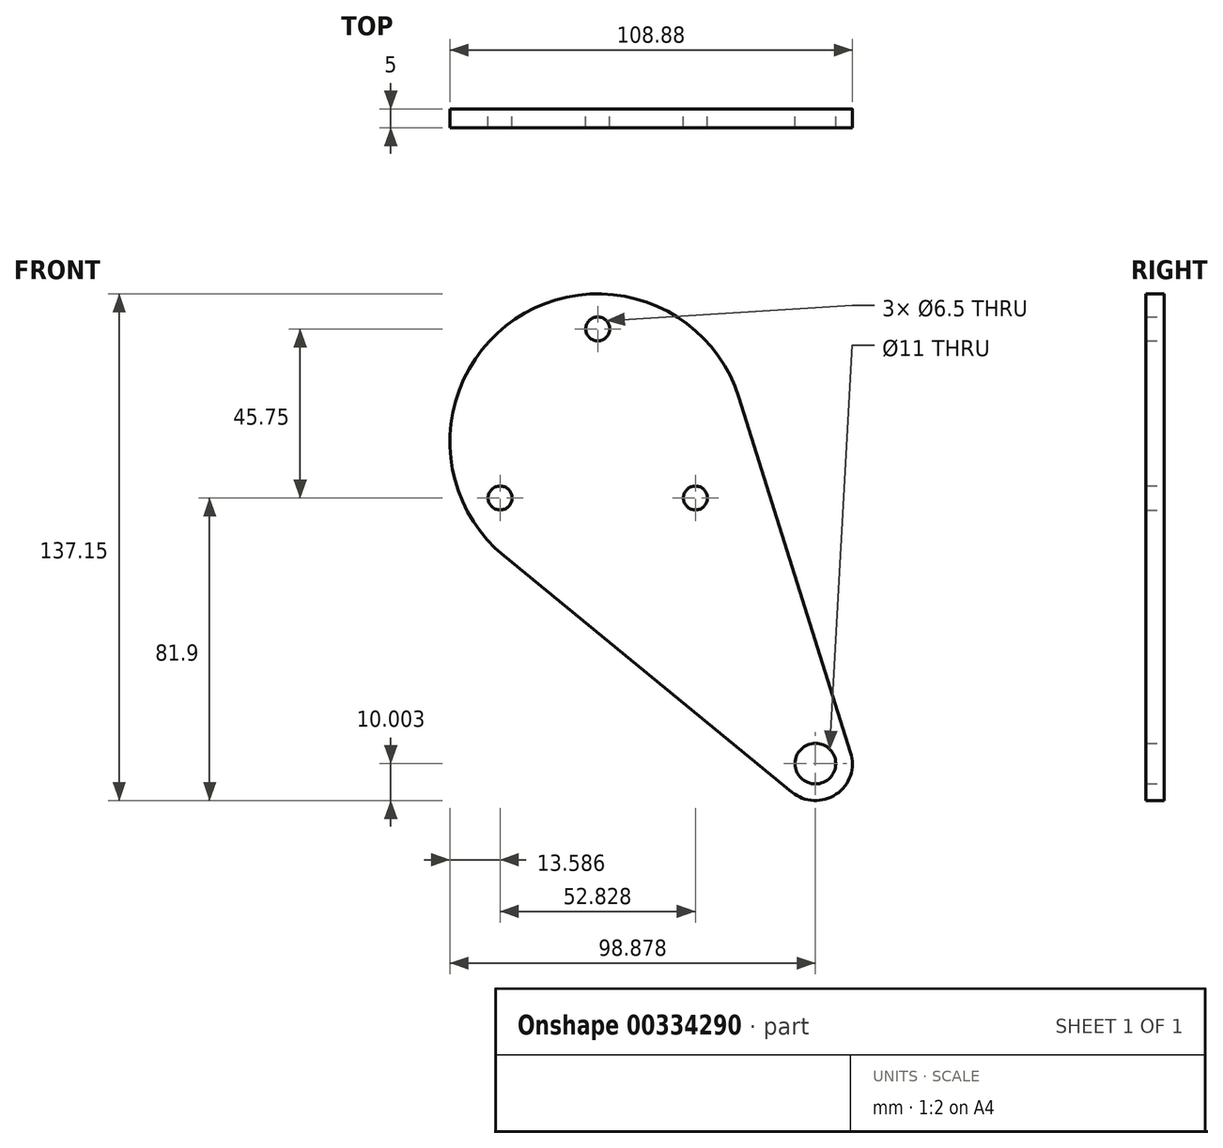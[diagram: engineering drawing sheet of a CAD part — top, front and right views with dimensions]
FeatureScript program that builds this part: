
annotation { "Feature Type Name" : "Feature", "Feature Type Description" : "" }
export const myFeature = defineFeature(function(context is Context, id is Id, definition is map)
    precondition{}
    {
        {
            var Q0;
            Q0=qCreatedBy(makeId("Front.planeOp"),FACE);
            var sketch = newSketch(context, id + "F0", { "sketchPlane" : qUnion([Q0])});
            skArc(sketch, "E0", {"start": v(38.15, 12) * mm, "mid": v(-22.4, 33.14) * mm, "end": v(-25.38, -30.92) * mm});
            skCircle(sketch, "E1", {"center": v(0, 0) * mm, "radius": 30.5 * mm, "construction": true});
            skCircle(sketch, "E2", {"center": v(0, 30.5) * mm, "radius": 3.25 * mm});
            skCircle(sketch, "E3.1.0", {"center": v(-26.41, -15.25) * mm, "radius": 3.25 * mm});
            skCircle(sketch, "E3.2.0", {"center": v(26.41, -15.25) * mm, "radius": 3.25 * mm});
            skLineSegment(sketch, "E4", {"start": v(0, 30.5) * mm, "end": v(0, 0) * mm, "construction": true});
            skLineSegment(sketch, "E5", {"start": v(0, 0) * mm, "end": v(26.41, -15.25) * mm, "construction": true});
            skLineSegment(sketch, "E6", {"start": v(0, 0) * mm, "end": v(-26.41, -15.25) * mm, "construction": true});
            skLineSegment(sketch, "E7", {"start": v(0, 0) * mm, "end": v(0, -60.86) * mm, "construction": true});
            skLineSegment(sketch, "E8", {"start": v(0, 0) * mm, "end": v(17.18, -59.9) * mm, "construction": true});
            skLineSegment(sketch, "E9", {"start": v(0, 0) * mm, "end": v(31.31, 8.98) * mm, "construction": true});
            skLineSegment(sketch, "E10", {"start": v(31.31, 8.98) * mm, "end": v(58.88, -87.15) * mm, "construction": true});
            skCircle(sketch, "E11", {"center": v(58.88, -87.15) * mm, "radius": 5.5 * mm});
            skArc(sketch, "E12", {"start": v(52.53, -94.88) * mm, "mid": v(64.48, -95.43) * mm, "end": v(68.42, -84.14) * mm});
            skLineSegment(sketch, "E13", {"start": v(68.42, -84.14) * mm, "end": v(38.15, 12) * mm});
            skLineSegment(sketch, "E14", {"start": v(52.53, -94.88) * mm, "end": v(-25.38, -30.92) * mm});
            skSolve(sketch);
        }
        {
            var Q0;
            Q0=qSketchRegion(id+"F0",true);
            extrude(context, id + "F1", {"entities" : qUnion([Q0]), "depth" : 5 * mm});
        }
    });
